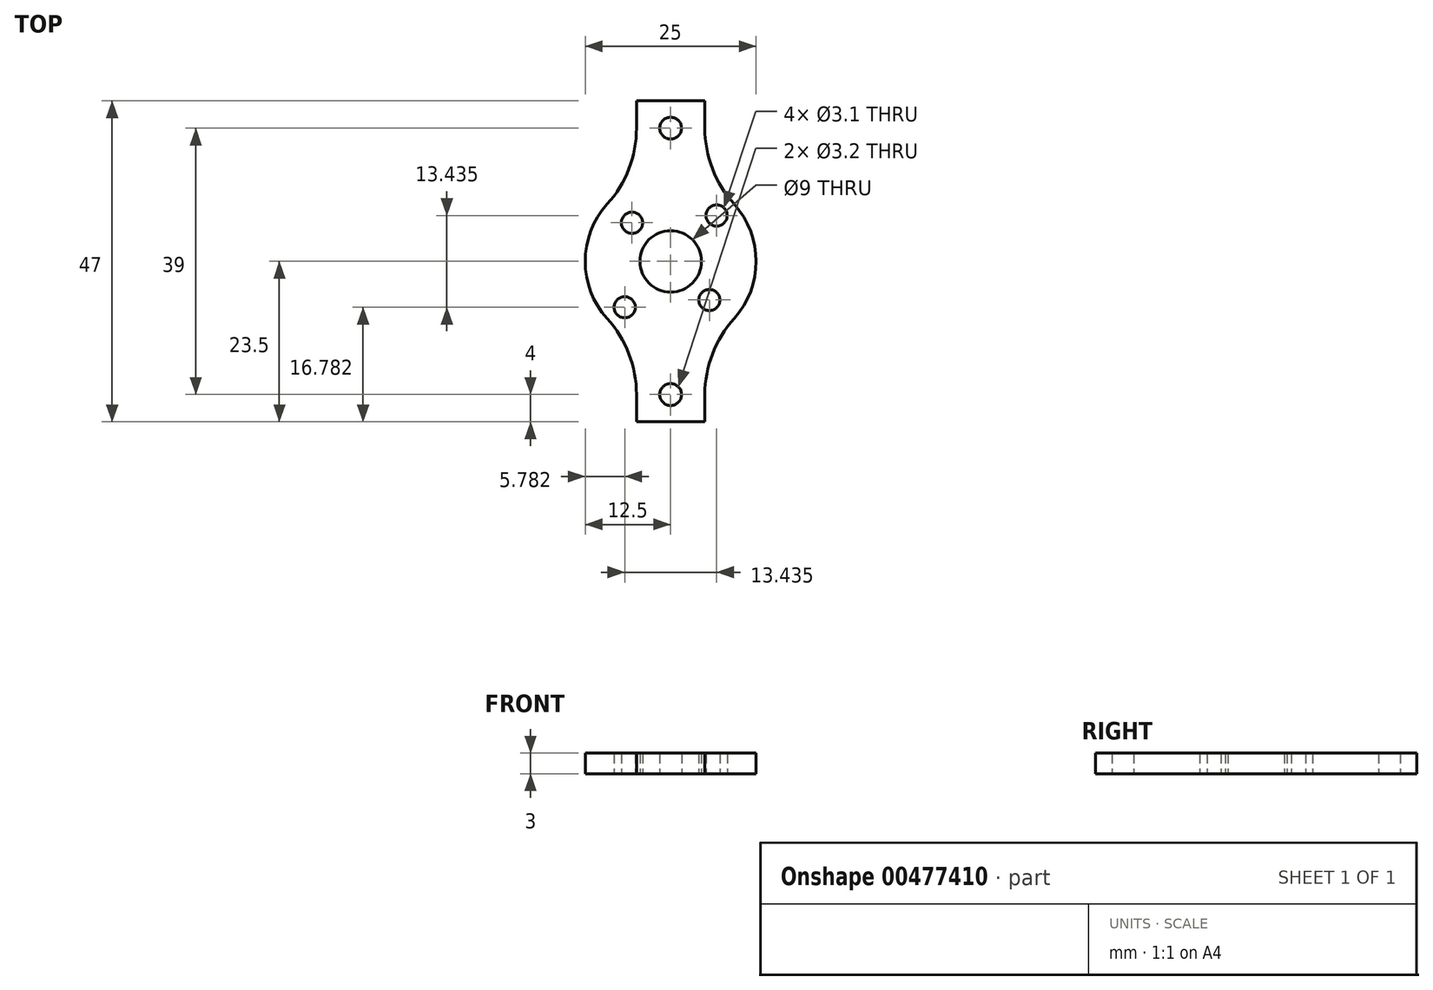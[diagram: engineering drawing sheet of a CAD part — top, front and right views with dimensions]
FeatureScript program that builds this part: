
annotation { "Feature Type Name" : "Feature", "Feature Type Description" : "" }
export const myFeature = defineFeature(function(context is Context, id is Id, definition is map)
    precondition{}
    {
        {
            var Q0;
            Q0=qCreatedBy(makeId("Top.planeOp"),FACE);
            var sketch = newSketch(context, id + "F0", { "sketchPlane" : qUnion([Q0])});
            skCircle(sketch, "E0", {"center": v(0, 0) * mm, "radius": 9.5 * mm, "construction": true});
            skCircle(sketch, "E1", {"center": v(6.72, 6.72) * mm, "radius": 1.55 * mm});
            skLineSegment(sketch, "E2", {"start": v(-12.5, 0) * mm, "end": v(12.5, 0) * mm, "construction": true});
            skLineSegment(sketch, "E3", {"start": v(0, 23.5) * mm, "end": v(0, -23.5) * mm, "construction": true});
            skCircle(sketch, "E4", {"center": v(0, 19.5) * mm, "radius": 1.6 * mm});
            skCircle(sketch, "E5.MirrorC", {"center": v(0, -19.5) * mm, "radius": 1.6 * mm});
            skLineSegment(sketch, "E6", {"start": v(6.72, 6.72) * mm, "end": v(0, 0) * mm, "construction": true});
            skLineSegment(sketch, "E7", {"start": v(0, 0) * mm, "end": v(-6.72, 6.72) * mm, "construction": true});
            skCircle(sketch, "E8.MirrorC", {"center": v(-6.72, -6.72) * mm, "radius": 1.55 * mm});
            skCircle(sketch, "E9", {"center": v(0, 0) * mm, "radius": 8 * mm, "construction": true});
            skCircle(sketch, "E10", {"center": v(-5.66, 5.66) * mm, "radius": 1.55 * mm});
            skCircle(sketch, "E11.MirrorC", {"center": v(5.66, -5.66) * mm, "radius": 1.55 * mm});
            skLineSegment(sketch, "E12", {"start": v(-5, 19.5) * mm, "end": v(-5, 19.5) * mm});
            skArc(sketch, "E13", {"start": v(-9.28, 8.38) * mm, "mid": v(-11.67, 4.49) * mm, "end": v(-12.5, 0) * mm});
            skArc(sketch, "E14", {"start": v(-9.28, 8.38) * mm, "mid": v(-6.1, 13.54) * mm, "end": v(-5, 19.5) * mm});
            skLineSegment(sketch, "E15", {"start": v(-12.5, 0) * mm, "end": v(-12.5, 0) * mm});
            skArc(sketch, "E16.MirrorCS", {"start": v(-9.28, -8.38) * mm, "mid": v(-11.67, -4.49) * mm, "end": v(-12.5, 0) * mm});
            skArc(sketch, "E17.MirrorCS", {"start": v(-9.28, -8.38) * mm, "mid": v(-6.1, -13.54) * mm, "end": v(-5, -19.5) * mm});
            skLineSegment(sketch, "E18.MirrorCS", {"start": v(-5, -19.5) * mm, "end": v(-5, -19.5) * mm});
            skLineSegment(sketch, "E19.MirrorCS", {"start": v(5, 19.5) * mm, "end": v(5, 19.5) * mm});
            skArc(sketch, "E20.MirrorCS", {"start": v(9.28, 8.38) * mm, "mid": v(6.1, 13.54) * mm, "end": v(5, 19.5) * mm});
            skArc(sketch, "E21.MirrorCS", {"start": v(9.28, 8.38) * mm, "mid": v(11.67, 4.49) * mm, "end": v(12.5, 0) * mm});
            skArc(sketch, "E22.MirrorCS", {"start": v(9.28, -8.38) * mm, "mid": v(11.67, -4.49) * mm, "end": v(12.5, 0) * mm});
            skArc(sketch, "E23.MirrorCS", {"start": v(9.28, -8.38) * mm, "mid": v(6.1, -13.54) * mm, "end": v(5, -19.5) * mm});
            skLineSegment(sketch, "E24.MirrorCS", {"start": v(5, -19.5) * mm, "end": v(5, -19.5) * mm});
            skCircle(sketch, "E25", {"center": v(0, 0) * mm, "radius": 4.5 * mm});
            skLineSegment(sketch, "E26", {"start": v(-5, 19.5) * mm, "end": v(-5, 23.5) * mm});
            skLineSegment(sketch, "E27", {"start": v(-5, 23.5) * mm, "end": v(5, 23.5) * mm});
            skLineSegment(sketch, "E28", {"start": v(5, 23.5) * mm, "end": v(5, 19.5) * mm});
            skLineSegment(sketch, "E29.MirrorCS", {"start": v(-5, -19.5) * mm, "end": v(-5, -23.5) * mm});
            skLineSegment(sketch, "E30.MirrorCS", {"start": v(-5, -23.5) * mm, "end": v(5, -23.5) * mm});
            skPoint(sketch, "E31.orphan", {"position": v(-5, -19.5) * mm});
            skPoint(sketch, "E32.orphan", {"position": v(0, -23.5) * mm});
            skPoint(sketch, "E33.MirrorCS.end.orphan", {"position": v(5, -19.5) * mm});
            skLineSegment(sketch, "E34.MirrorCS", {"start": v(5, -23.5) * mm, "end": v(5, -19.5) * mm});
            skSolve(sketch);
        }
        {
            var Q0;
            Q0=makeQuery(id+"F0.imprint","IMPRINT",FACE,{"disambiguationData":[TD([[makeQuery(id+"F0.imprint","IMPRINT",EDGE,{"derivedFrom":sQuery(id+"F0.wireOp",EDGE,"E1")}),-1.0]])]});
            extrude(context, id + "F1", {"entities" : qUnion([Q0]), "depth" : 3 * mm});
        }
    });
